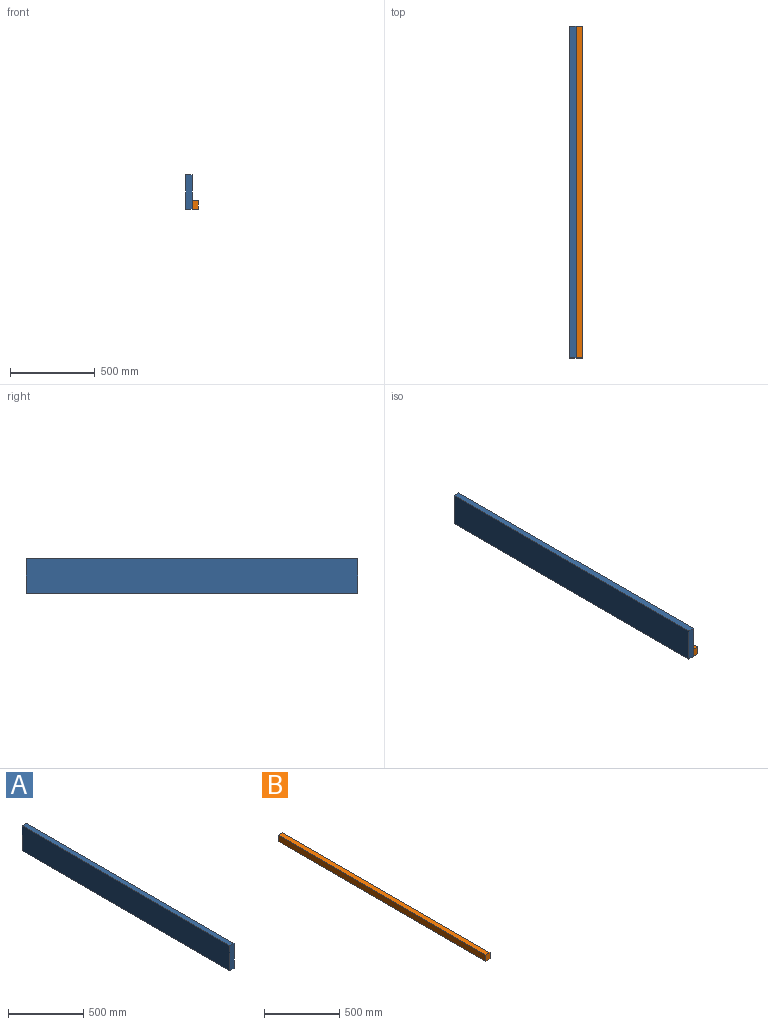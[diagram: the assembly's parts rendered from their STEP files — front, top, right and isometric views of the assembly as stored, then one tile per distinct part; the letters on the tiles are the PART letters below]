
ASSEMBLY  parts=2 mates=1
PART A: 6 faces, bbox 38.1x1955.8x203.2 mm
  f0: plane 1955.8x203.2mm, normal (-1,0,0), area 397418.6mm2, adj f1,f3,f4,f5
  f1: plane 1955.8x38.1mm, normal (0,0,-1), area 74516mm2, adj f0,f2,f4,f5
  f2: plane 1955.8x203.2mm, normal (1,0,0), area 397418.6mm2, adj f1,f3,f4,f5
  f3: plane 1955.8x38.1mm, normal (0,0,1), area 74516mm2, adj f0,f2,f4,f5
  f4: plane 203.2x38.1mm, normal (0,-1,0), area 7741.9mm2, adj f0,f1,f2,f3
  f5: plane 203.2x38.1mm, normal (0,1,0), area 7741.9mm2, adj f0,f1,f2,f3
PART B: 6 faces, bbox 38.1x1955.8x50.8 mm
  f0: plane 1955.8x50.8mm, normal (-1,0,0), area 99354.6mm2, adj f1,f3,f4,f5
  f1: plane 1955.8x38.1mm, normal (0,0,-1), area 74516mm2, adj f0,f2,f4,f5
  f2: plane 1955.8x50.8mm, normal (1,0,0), area 99354.6mm2, adj f1,f3,f4,f5
  f3: plane 1955.8x38.1mm, normal (0,0,1), area 74516mm2, adj f0,f2,f4,f5
  f4: plane 50.8x38.1mm, normal (0,-1,0), area 1935.5mm2, adj f0,f1,f2,f3
  f5: plane 50.8x38.1mm, normal (0,1,0), area 1935.5mm2, adj f0,f1,f2,f3
PLACE A t=(-19.05,977.9,0)mm
PLACE B rot(axis=(0,0,1),180deg) t=(57.15,-977.9,0)mm
MATE fastened A.f2 <-> B.f2  axis (1,0,0) through (19.05,0,0)mm
